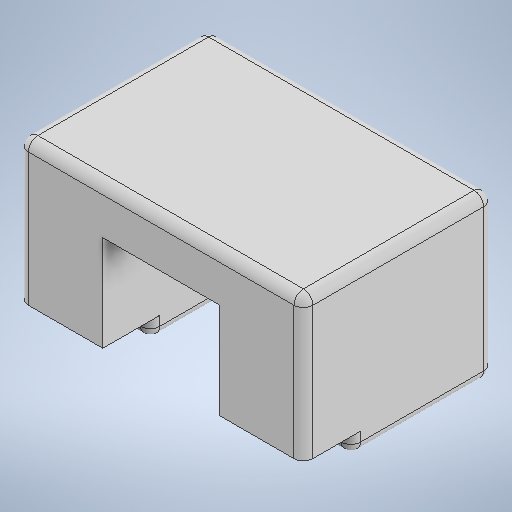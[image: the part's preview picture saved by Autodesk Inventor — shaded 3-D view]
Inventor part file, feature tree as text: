
AUTODESK INVENTOR PART (.ipt)
format: ipt  version: 2025 (Build 290162000, 162)  size: 361,472 bytes
history: native  units: in
note: dims shown in document units (in); Inventor stores cm internally (conversion verified against a paired STEP export)
features: projected_geometry x6, extrude x5, sketch x4, fillet x4, chamfer x2
ambient origin geometry x8: Origin, YZ Plane, XZ Plane, XY Plane, X Axis, Y Axis, Z Axis, Center Point
bodies: Solid1 (feature_tree)
feature tree (21):
  sketch  "Sketch1"  dims[d0=0.4843in d1=1.1811in]
  extrude  "Extrusion1"  Depth=1.1811in
  extrude  "Extrusion4"  Depth=0.5906in
  extrude  "Extrusion2"  Depth=0.1181in
  extrude  "Extrusion3"  Depth=0.1181in
  fillet  "Fillet1"  Radius=0.3937in
  extrude  "Extrusion5"  Depth=0.0394in
  chamfer  "Chamfer1"  Distance=0.5906in
  chamfer  "Chamfer2"  Distance=0.0394in
  fillet  "Fillet2"  Radius=0.0394in
  fillet  "Fillet3"  Radius=0.0945in
  fillet  "Fillet4"  Radius=0.0315in
  sketch  "Sketch2"  dims[d2=0.5906in d3=0.3976in]
  projected_geometry  "Projected Loop1"
  sketch  "Sketch3"  dims[d4=0.7874in d5=0.0in d6=0.1181in]
  projected_geometry  "Projected Loop2"
  projected_geometry  "Projected Loop3"
  projected_geometry  "Projected Loop4"
  projected_geometry  "Projected Loop5"
  sketch  "Sketch4"  dims[d7=0.3937in d8=0.0in d9=0.1181in d10=0.3937in d11=0.0in d12=0.0787in d13=0.5906in d14=0.0in d15=0.0394in d16=0.0394in d17=0.0945in d18=0.0315in d19=0.0787in d20=0.2362in d21=0.1181in d22=0.0in d23=0.0984in d24=0.125in d25=45.0deg d26=0.0394in d27=0.125in d28=45.0deg d29=0.0394in d30=0.0197in d31=0.0394in]
  projected_geometry  "Projected Loop6"
